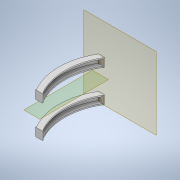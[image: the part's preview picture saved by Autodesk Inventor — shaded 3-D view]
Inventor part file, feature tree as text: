
AUTODESK INVENTOR PART (.ipt)
format: ipt  version: 2021 (Build 250183000, 183)  size: 167,936 bytes
history: native  units: mm
features: sketch x3, plane x2, mirror x2, sweep x1, extrude x1, projected_geometry x1
ambient origin geometry x8: Origin, YZ Plane, XZ Plane, XY Plane, X Axis, Y Axis, Z Axis, Center Point
bodies: Solid1 (feature_tree)
feature tree (10):
  sketch  "Sketch1"  dims[d0=100.0mm d1=7.0mm]
  plane  "Work Plane1"
  sweep  "Sweep1"
  extrude  "Extrusion1"  Depth=1.0mm
  mirror  "Mirror1"
  plane  "Work Plane2"
  mirror  "Mirror2"
  sketch  "Sketch2"  dims[d2=9.0mm d3=1.0mm]
  sketch  "Sketch3"  dims[d4=9.0mm d5=1.0mm d14=0.0mm d15=0.0mm d16=0.5mm d17=1.0mm d18=0.0mm d19=10.0mm]
  projected_geometry  "Projected Loop1"
